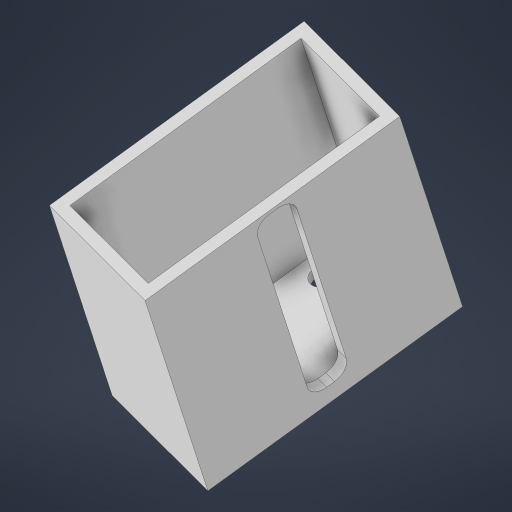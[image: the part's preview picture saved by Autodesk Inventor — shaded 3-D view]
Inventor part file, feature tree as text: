
AUTODESK INVENTOR PART (.ipt)
format: ipt  version: 2023 (Build 270158000, 158)  size: 204,800 bytes
history: native  units: mm
features: extrude x3, sketch x3, shell x1
ambient origin geometry x8: Origin, YZ Plane, XZ Plane, XY Plane, X Axis, Y Axis, Z Axis, Center Point
bodies: Solid1 (feature_tree)
feature tree (7):
  extrude  "Extrusion1"  Depth=33.0mm
  shell  "Shell1"  Thickness=66.0mm
  extrude  "Extrusion2"  Depth=10.0mm
  extrude  "Extrusion3"  Depth=5.0mm
  sketch  "Sketch1"  dims[d0=65.0mm d1=33.0mm d2=66.0mm d3=0.0mm]
  sketch  "Sketch2"  dims[d4=3.0mm d5=10.0mm]
  sketch  "Sketch3"  dims[d6=60.0mm d7=5.0mm d8=10.0mm d9=0.0mm d10=4.0mm d11=5.0mm d12=5.0mm d13=5.0mm d14=5.0mm d15=8.0mm d16=8.0mm d17=30.0mm d18=15.0mm d19=0.0mm d20=0.0mm]
